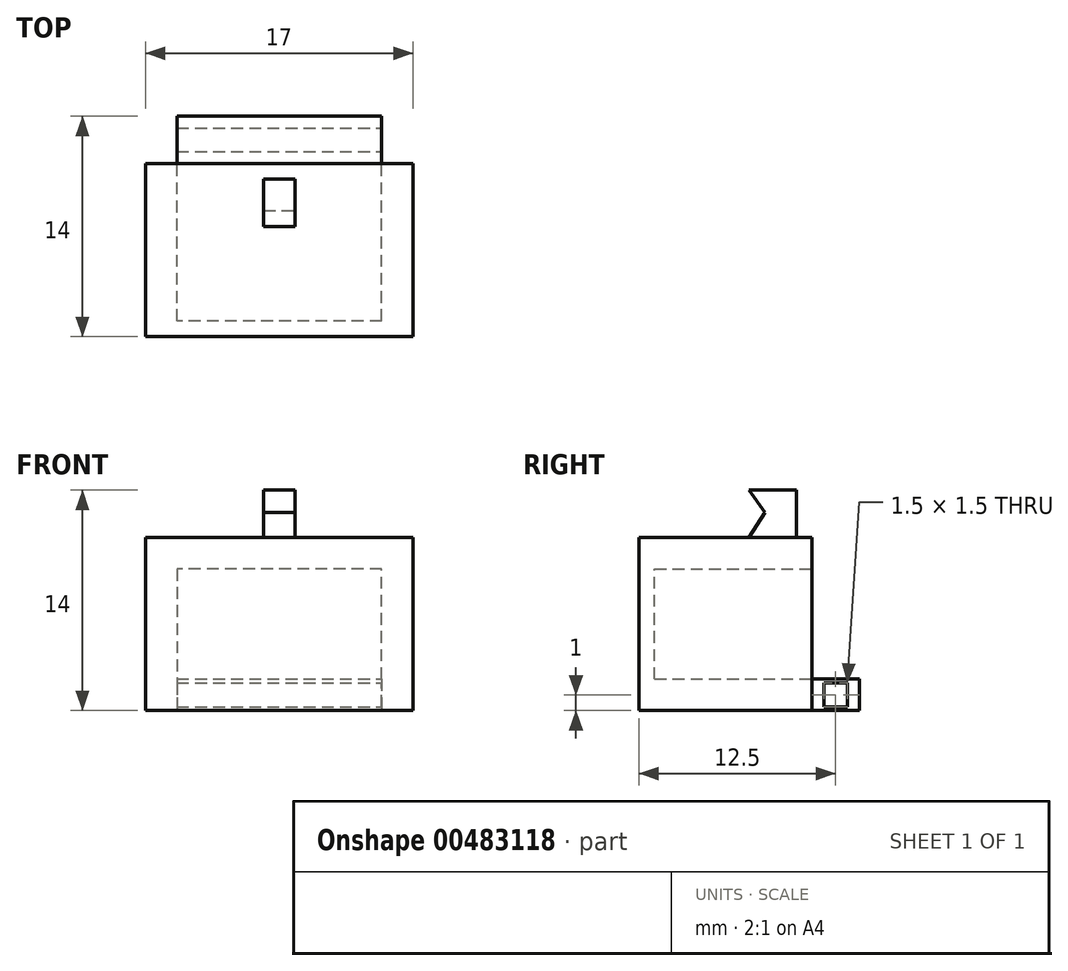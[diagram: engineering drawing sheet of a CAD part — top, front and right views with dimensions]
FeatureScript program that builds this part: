
annotation { "Feature Type Name" : "Feature", "Feature Type Description" : "" }
export const myFeature = defineFeature(function(context is Context, id is Id, definition is map)
    precondition{}
    {
        {
            var Q0;
            Q0=qCreatedBy(makeId("Top.planeOp"),FACE);
            var sketch = newSketch(context, id + "F0", { "sketchPlane" : qUnion([Q0])});
            skLineSegment(sketch, "E0.bottom", {"start": v(9.85, -5.5) * mm, "end": v(-7.15, -5.5) * mm});
            skLineSegment(sketch, "E0.top", {"start": v(9.85, 5.5) * mm, "end": v(-7.15, 5.5) * mm});
            skLineSegment(sketch, "E0.left", {"start": v(9.85, -5.5) * mm, "end": v(9.85, 5.5) * mm});
            skLineSegment(sketch, "E0.right", {"start": v(-7.15, -5.5) * mm, "end": v(-7.15, 5.5) * mm});
            skPoint(sketch, "E0.middle", {"position": v(1.35, 0) * mm});
            skSolve(sketch);
        }
        {
            var Q0;
            Q0=makeQuery(id+"F0.imprint","IMPRINT",FACE,{"disambiguationData":[TD([[makeQuery(id+"F0.imprint","IMPRINT",EDGE,{"derivedFrom":sQuery(id+"F0.wireOp",EDGE,"E0.bottom")}),-1.0]])]});
            extrude(context, id + "F1", {"entities" : qUnion([Q0]), "depth" : 11 * mm});
        }
        {
            var Q0;
            Q0=makeQuery(id+"F1.opExtrude","SWEPT_FACE",FACE,{"disambiguationData":[OSD([sQuery(id+"F0.wireOp",EDGE,"E0.top")])]});
            var sketch = newSketch(context, id + "F2", { "sketchPlane" : qUnion([Q0])});
            skLineSegment(sketch, "E1", {"start": v(-1.35, 0) * mm, "end": v(-1.35, 2) * mm});
            skLineSegment(sketch, "E2", {"start": v(-1.35, 11) * mm, "end": v(-1.35, 9) * mm});
            skLineSegment(sketch, "E3", {"start": v(7.15, 5.5) * mm, "end": v(5.15, 5.5) * mm});
            skLineSegment(sketch, "E4", {"start": v(-9.85, 5.5) * mm, "end": v(-7.85, 5.5) * mm});
            skLineSegment(sketch, "E5", {"start": v(5.15, 2) * mm, "end": v(-7.85, 2) * mm});
            skLineSegment(sketch, "E6", {"start": v(-7.85, 2) * mm, "end": v(-7.85, 9) * mm});
            skLineSegment(sketch, "E7", {"start": v(-7.85, 9) * mm, "end": v(5.15, 9) * mm});
            skLineSegment(sketch, "E8", {"start": v(5.15, 9) * mm, "end": v(5.15, 2) * mm});
            skSolve(sketch);
        }
        {
            var Q0;
            {var subQ4=sQuery(id+"F2.wireOp",EDGE,"E5");var subQ6=makeQuery(id+"F2.imprint","INTERSECT",VERTEX,{"derivedFrom":[sQuery(id+"F2.wireOp",EDGE,"E1"),subQ4]});Q0=makeQuery(id+"F2.imprint","IMPRINT",FACE,{"disambiguationData":[TD([[makeQuery(id+"F2.imprint","IMPRINT",EDGE,{"disambiguationData":[TD([[subQ6,1.0]])],"derivedFrom":subQ4}),-1.0]])]});}
            extrude(context, id + "F3", {"entities" : qUnion([Q0]), "operationType" : NewBodyOperationType.REMOVE, "oppositeDirection" : true, "depth" : 10 * mm});
        }
        {
            var Q0;
            Q0=makeQuery(id+"F1.opExtrude","SWEPT_FACE",FACE,{"disambiguationData":[OSD([sQuery(id+"F0.wireOp",EDGE,"E0.top")])]});
            var sketch = newSketch(context, id + "F4", { "sketchPlane" : qUnion([Q0])});
            skLineSegment(sketch, "E9", {"start": v(-7.85, 2) * mm, "end": v(-7.85, 0) * mm});
            skLineSegment(sketch, "E10", {"start": v(5.15, 2) * mm, "end": v(5.15, 0) * mm});
            skSolve(sketch);
        }
        {
            var Q0;
            Q0=makeQuery(id+"F4.imprint","IMPRINT",FACE,{"disambiguationData":[TD([[makeQuery(id+"F4.imprint","IMPRINT",EDGE,{"derivedFrom":sQuery(id+"F4.wireOp",EDGE,"c3mefccv-YEB7-Yrey-FmsH-Wu1tvEkqzDn3")}),-1.0]])]});
            var Q1;
            {var subQ0=sQuery(id+"F4.wireOp",EDGE,"E9");Q1=makeQuery(id+"F4.imprint","IMPRINT",FACE,{"disambiguationData":[TD([[makeQuery(id+"F4.imprint","IMPRINT",EDGE,{"derivedFrom":subQ0}),1.0]])]});}
            extrude(context, id + "F5", {"entities" : qUnion([Q0, Q1]), "operationType" : NewBodyOperationType.ADD, "depth" : 3 * mm});
        }
        {
            var Q0;
            Q0=makeQuery(id+"F5.opExtrude","SWEPT_FACE",FACE,{"disambiguationData":[OSD([sQuery(id+"F4.wireOp",EDGE,"E9")])]});
            var sketch = newSketch(context, id + "F6", { "sketchPlane" : qUnion([Q0])});
            skLineSegment(sketch, "E11.bottom", {"start": v(8.5, 2) * mm, "end": v(5.5, 2) * mm});
            skLineSegment(sketch, "E11.top", {"start": v(8.5, 0) * mm, "end": v(5.5, 0) * mm});
            skLineSegment(sketch, "E11.left", {"start": v(8.5, 2) * mm, "end": v(8.5, 0) * mm});
            skLineSegment(sketch, "E11.right", {"start": v(5.5, 2) * mm, "end": v(5.5, 0) * mm});
            skLineSegment(sketch, "E12.bottom", {"start": v(7.75, 0.25) * mm, "end": v(6.25, 0.25) * mm});
            skLineSegment(sketch, "E12.top", {"start": v(7.75, 1.75) * mm, "end": v(6.25, 1.75) * mm});
            skLineSegment(sketch, "E12.left", {"start": v(7.75, 0.25) * mm, "end": v(7.75, 1.75) * mm});
            skLineSegment(sketch, "E12.right", {"start": v(6.25, 0.25) * mm, "end": v(6.25, 1.75) * mm});
            skPoint(sketch, "E12.middle", {"position": v(7, 1) * mm});
            skPoint(sketch, "E12.middle.positionSnap0", {"position": v(7, 2) * mm});
            skPoint(sketch, "E12.middle.positionSnap1", {"position": v(8.5, 1) * mm});
            skPoint(sketch, "E12.centerSnap0", {"position": v(7, 2) * mm});
            skPoint(sketch, "E12.centerSnap1", {"position": v(8.5, 1) * mm});
            skSolve(sketch);
        }
        {
            var Q0;
            Q0=makeQuery(id+"F6.imprint","IMPRINT",FACE,{"disambiguationData":[TD([[makeQuery(id+"F6.imprint","IMPRINT",EDGE,{"derivedFrom":sQuery(id+"F6.wireOp",EDGE,"E12.bottom")}),-1.0]])]});
            extrude(context, id + "F7", {"entities" : qUnion([Q0]), "operationType" : NewBodyOperationType.REMOVE, "endBound" : BoundingType.THROUGH_ALL, "oppositeDirection" : true, "depth" : 25 * mm});
        }
        {
            var Q0;
            Q0=makeQuery(id+"F1.opExtrude","CAP_FACE",FACE,{"disambiguationData":[OSD([sQuery(id+"F0.wireOp",EDGE,"E0.bottom"),sQuery(id+"F0.wireOp",EDGE,"E0.top"),sQuery(id+"F0.wireOp",EDGE,"E0.left"),sQuery(id+"F0.wireOp",EDGE,"E0.right")])],"isStart":false});
            var sketch = newSketch(context, id + "F8", { "sketchPlane" : qUnion([Q0])});
            skLineSegment(sketch, "E13.bottom", {"start": v(2.35, 3.5) * mm, "end": v(0.35, 3.5) * mm});
            skLineSegment(sketch, "E13.top", {"start": v(2.35, 1.5) * mm, "end": v(0.35, 1.5) * mm});
            skLineSegment(sketch, "E13.left", {"start": v(2.35, 3.5) * mm, "end": v(2.35, 1.5) * mm});
            skLineSegment(sketch, "E13.right", {"start": v(0.35, 3.5) * mm, "end": v(0.35, 1.5) * mm});
            skPoint(sketch, "E13.middle", {"position": v(1.35, 2.5) * mm});
            skSolve(sketch);
        }
        {
            var Q0;
            Q0=makeQuery(id+"F8.imprint","IMPRINT",FACE,{"disambiguationData":[TD([[makeQuery(id+"F8.imprint","IMPRINT",EDGE,{"derivedFrom":sQuery(id+"F8.wireOp",EDGE,"E13.bottom")}),1.0]])]});
            extrude(context, id + "F9", {"entities" : qUnion([Q0]), "operationType" : NewBodyOperationType.ADD, "depth" : 3 * mm});
        }
        {
            var Q0;
            Q0=makeQuery(id+"F9.opExtrude","SWEPT_FACE",FACE,{"disambiguationData":[OSD([sQuery(id+"F8.wireOp",EDGE,"E13.left")])]});
            var sketch = newSketch(context, id + "F10", { "sketchPlane" : qUnion([Q0])});
            skLineSegment(sketch, "E14", {"start": v(1.5, 14) * mm, "end": v(2.5, 12.6) * mm});
            skLineSegment(sketch, "E15", {"start": v(2.5, 12.6) * mm, "end": v(1.5, 11) * mm});
            skSolve(sketch);
        }
        {
            var Q0;
            Q0=makeQuery(id+"F10.imprint","IMPRINT",FACE,{"disambiguationData":[TD([[makeQuery(id+"F10.imprint","IMPRINT",EDGE,{"derivedFrom":sQuery(id+"F10.wireOp",EDGE,"E14")}),-1.0]])]});
            extrude(context, id + "F11", {"entities" : qUnion([Q0]), "operationType" : NewBodyOperationType.REMOVE, "endBound" : BoundingType.THROUGH_ALL, "oppositeDirection" : true, "depth" : 25 * mm});
        }
        {
            var Q0;
            Q0=makeQuery(id+"F9.opExtrude","SWEPT_FACE",FACE,{"disambiguationData":[OSD([sQuery(id+"F8.wireOp",EDGE,"E13.bottom")])]});
            extrude(context, id + "F12", {"entities" : qUnion([Q0]), "operationType" : NewBodyOperationType.ADD, "depth" : 1 * mm});
        }
    });
